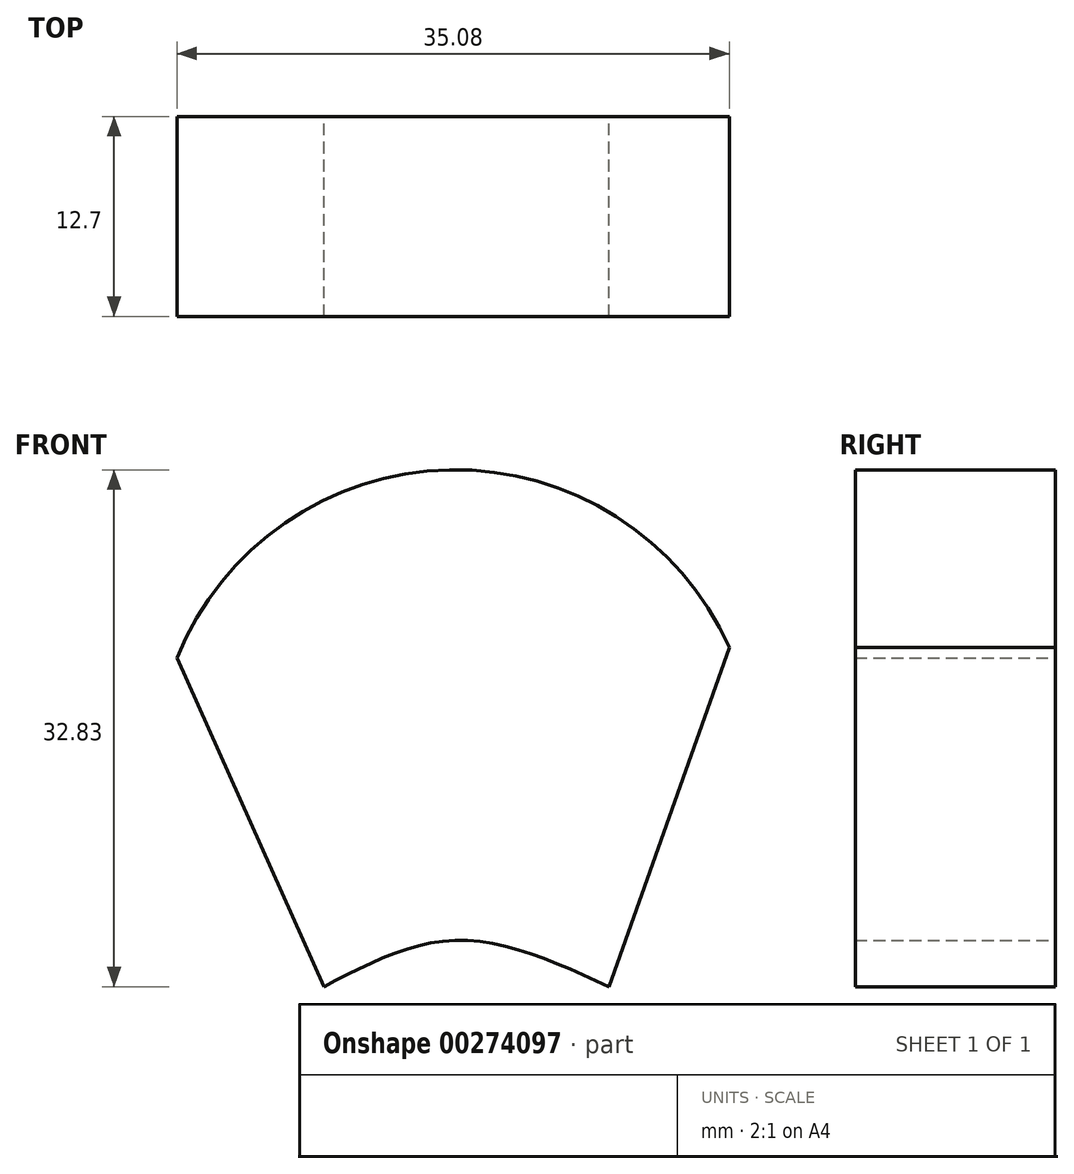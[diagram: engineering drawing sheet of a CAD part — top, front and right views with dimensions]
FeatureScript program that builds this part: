
annotation { "Feature Type Name" : "Feature", "Feature Type Description" : "" }
export const myFeature = defineFeature(function(context is Context, id is Id, definition is map)
    precondition{}
    {
        {
            var Q0;
            Q0=qCreatedBy(makeId("Front.planeOp"),FACE);
            var sketch = newSketch(context, id + "F0", { "sketchPlane" : qUnion([Q0])});
            skArc(sketch, "E0", {"start": v(7.64, 7.77) * mm, "mid": v(-10.13, 19.05) * mm, "end": v(-27.44, 7.09) * mm});
            skLineSegment(sketch, "E1", {"start": v(7.64, 7.77) * mm, "end": v(0, -13.78) * mm});
            skLineSegment(sketch, "E2", {"start": v(-27.44, 7.09) * mm, "end": v(-18.1, -13.78) * mm});
            skFitSpline(sketch, "E3", {"points": [v(-18.1, -13.78) * mm, v(-9.65, -10.83) * mm, v(0, -13.78) * mm], "startDerivative": vector(17.12, 8.93) * mm, "endDerivative": vector(19.07, -8.76) * mm});
            skSolve(sketch);
        }
        {
            var Q0;
            Q0 = qSketchRegion(id + "F0", true);
            extrude(context, id + "F1", {"entities" : qUnion([Q0]), "depth" : 12.7 * mm});
        }
    });
